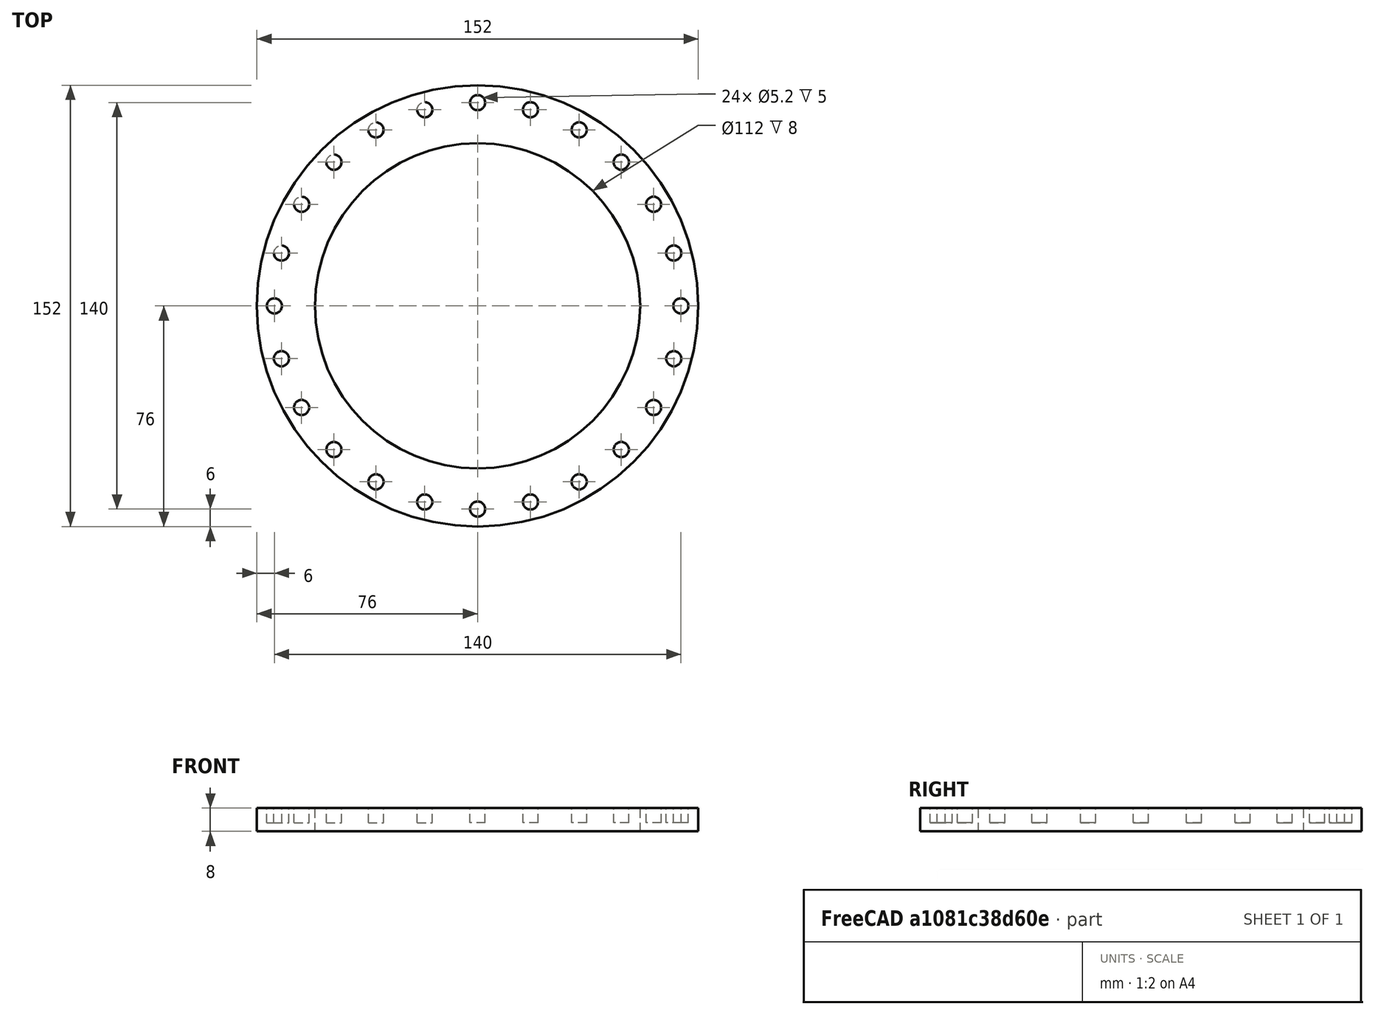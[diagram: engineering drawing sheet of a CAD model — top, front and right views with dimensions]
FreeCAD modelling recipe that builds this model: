
FCSTD DOCUMENT
Label: rat.social.interaction.chamber
objects: Part::Cylinder×9, Part::Mirroring×5, Part::Cut×2, Part::MultiFuse×2
note: 18 computed .brp shape members not serialized (recipe doc carries the construction recipe); baked Part::Feature solids carry a one-line shape summary decoded from their .brp

FEATURE [Part::Cylinder] Cylinder
  Angle = 360
  Height = 8
  Radius = 76
FEATURE [Part::Cylinder] Cylinder001  label="pole1"
  Angle = 360
  Height = 20
  Placement = pos=(70,0,3) rot=(0,0,1;0rad)
  Radius = 2.6
FEATURE [Part::Cylinder] Cylinder002
  Angle = 360
  Height = 10
  Radius = 56
FEATURE [Part::Cut] Cut
  Base = -> Cylinder
  Tool = -> Cylinder002
FEATURE [Part::Cylinder] Cylinder001001
  Angle = 360
  Height = 20
  Placement = pos=(0,70,3) rot=(0,0,1;0rad)
  Radius = 2.6
FEATURE [Part::Cylinder] Cylinder001002
  Angle = 360
  Height = 20
  Placement = pos=(18.2,67.55,3) rot=(0,0,1;0rad)
  Radius = 2.6
FEATURE [Part::Cylinder] Cylinder001002001  label="pole2"
  Angle = 360
  Height = 20
  Placement = pos=(67.55,18.2,3) rot=(0,0,1;0rad)
  Radius = 2.6
FEATURE [Part::Cylinder] Cylinder001002001001  label="pole003"
  Angle = 360
  Height = 20
  Placement = pos=(60.62,35,3) rot=(0,0,1;0rad)
  Radius = 2.6
FEATURE [Part::Cylinder] Cylinder001002001001001  label="pole004"
  Angle = 360
  Height = 20
  Placement = pos=(49.49,49.49,3) rot=(0,0,1;0rad)
  Radius = 2.6
FEATURE [Part::Cylinder] Cylinder001002001001001001  label="pole005"
  Angle = 360
  Height = 26
  Placement = pos=(35,60.62,3) rot=(0,0,1;0rad)
  Radius = 2.6
FEATURE [Part::MultiFuse] Fusion
  Shapes = -> [Cylinder001002001,Cylinder001002001001,Cylinder001002001001001,Cylinder001002001001001001,Cylinder001002]
FEATURE [Part::Mirroring] Part__Mirroring  label="Fusion (Mirror #1)"
  Base = (0,0,0)
  Normal = (0,1,0)
  Source = -> Fusion
FEATURE [Part::Mirroring] Part__Mirroring001  label="Fusion (Mirror #2)"
  Base = (2.86102e-06,42.7668,16)
  Normal = (1,0,-1.19209e-07)
  Source = -> Fusion
FEATURE [Part::Mirroring] Part__Mirroring002  label="Fusion (Mirror #3)"
  Base = (0,0,0)
  Normal = (1,0,0)
  Source = -> Part__Mirroring
FEATURE [Part::Mirroring] Part__Mirroring003  label="pole1 (Mirror #4)"
  Base = (0,0,0)
  Normal = (1,0,0)
  Source = -> Cylinder001
FEATURE [Part::Mirroring] Part__Mirroring004  label="Cylinder001001 (Mirror #5)"
  Base = (0,0,0)
  Normal = (0,1,0)
  Source = -> Cylinder001001
FEATURE [Part::MultiFuse] Fusion001
  Shapes = -> [Cylinder001001,Part__Mirroring,Cylinder001,Fusion,Cylinder001002001,Cylinder001002001001,Cylinder001002001001001,Cylinder001002001001001001,Cylinder001002,Part__Mirroring001,Part__Mirroring003,Part__Mirroring002,Part__Mirroring004]
FEATURE [Part::Cut] Cut001
  Base = -> Cut
  Tool = -> Fusion001
